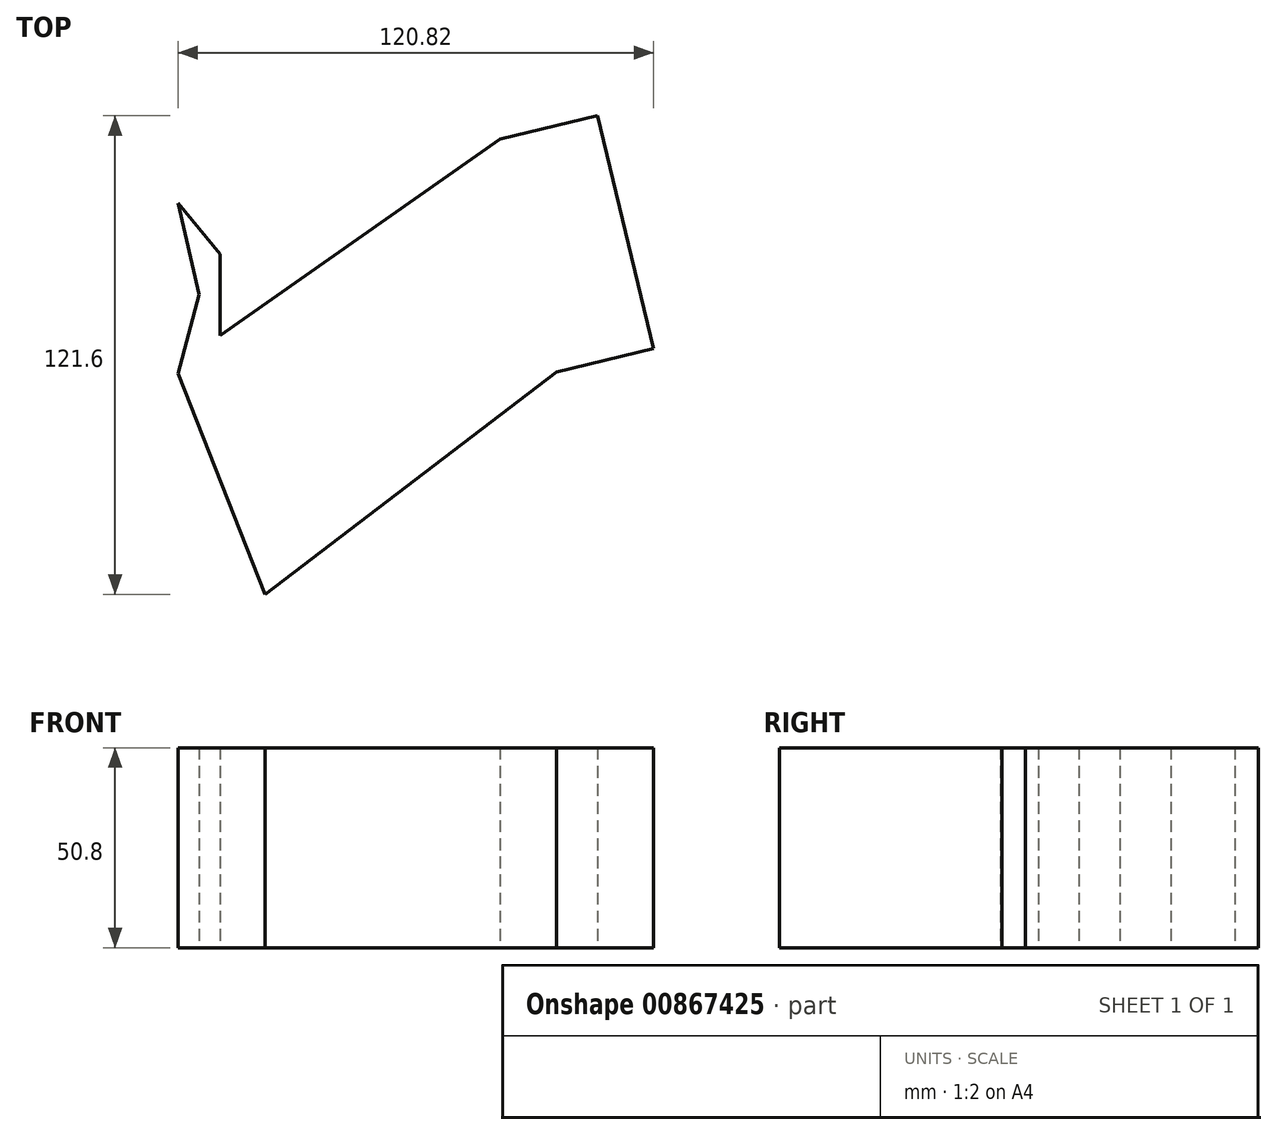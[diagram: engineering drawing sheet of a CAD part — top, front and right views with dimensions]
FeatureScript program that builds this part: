
annotation { "Feature Type Name" : "Feature", "Feature Type Description" : "" }
export const myFeature = defineFeature(function(context is Context, id is Id, definition is map)
    precondition{}
    {
        {
            var Q0;
            Q0=qCreatedBy(makeId("Top.planeOp"),FACE);
            var sketch = newSketch(context, id + "F0", { "sketchPlane" : qUnion([Q0])});
            skLineSegment(sketch, "E0", {"start": v(0, 42.38) * mm, "end": v(22.1, -13.77) * mm});
            skLineSegment(sketch, "E1", {"start": v(22.1, -13.77) * mm, "end": v(96.13, 42.73) * mm});
            skLineSegment(sketch, "E2", {"start": v(96.13, 42.73) * mm, "end": v(81.85, 101.87) * mm});
            skLineSegment(sketch, "E3", {"start": v(81.85, 101.87) * mm, "end": v(10.71, 52) * mm});
            skLineSegment(sketch, "E4", {"start": v(10.71, 52) * mm, "end": v(10.71, 72.68) * mm});
            skLineSegment(sketch, "E5", {"start": v(10.71, 72.68) * mm, "end": v(0, 85.64) * mm});
            skLineSegment(sketch, "E6", {"start": v(0, 85.64) * mm, "end": v(5.36, 62.34) * mm});
            skPoint(sketch, "E6.endSnap0", {"position": v(10.71, 62.34) * mm});
            skPoint(sketch, "E6.endSnap1", {"position": v(5.36, 79.16) * mm});
            skLineSegment(sketch, "E7", {"start": v(5.36, 62.34) * mm, "end": v(0, 42.38) * mm});
            skSolve(sketch);
        }
        {
            var Q0;
            Q0 = qSketchRegion(id + "F0", true);
            extrude(context, id + "F1", {"entities" : qUnion([Q0]), "depth" : 25.4 * mm, "offsetDistance" : 25.4 * mm});
        }
        {
            var Q0;
            Q0=makeQuery(id+"F1.opExtrude","CAP_FACE",FACE,{"disambiguationData":[OSD([sQuery(id+"F0.wireOp",EDGE,"E0"),sQuery(id+"F0.wireOp",EDGE,"E1"),sQuery(id+"F0.wireOp",EDGE,"E2"),sQuery(id+"F0.wireOp",EDGE,"E3"),sQuery(id+"F0.wireOp",EDGE,"E4"),sQuery(id+"F0.wireOp",EDGE,"E5"),sQuery(id+"F0.wireOp",EDGE,"E6"),sQuery(id+"F0.wireOp",EDGE,"E7")])],"isStart":false});
            extrude(context, id + "F2", {"entities" : qUnion([Q0]), "operationType" : NewBodyOperationType.ADD, "depth" : 25.4 * mm, "offsetDistance" : 25.4 * mm});
        }
        {
            var Q0;
            {var subQ0=sQuery(id+"F0.wireOp",EDGE,"E2");Q0=makeQuery(id+"F2.boolean.opBoolean","MERGE",FACE,{"derivedFrom":[makeQuery(id+"F1.opExtrude","SWEPT_FACE",FACE,{"disambiguationData":[OSD([subQ0])]}),makeQuery(id+"F2.opExtrude","SWEPT_FACE",FACE,{"disambiguationData":[OSD([subQ0])]})]});}
            extrude(context, id + "F3", {"entities" : qUnion([Q0]), "operationType" : NewBodyOperationType.ADD, "depth" : 25.4 * mm, "offsetDistance" : 25.4 * mm});
        }
    });
